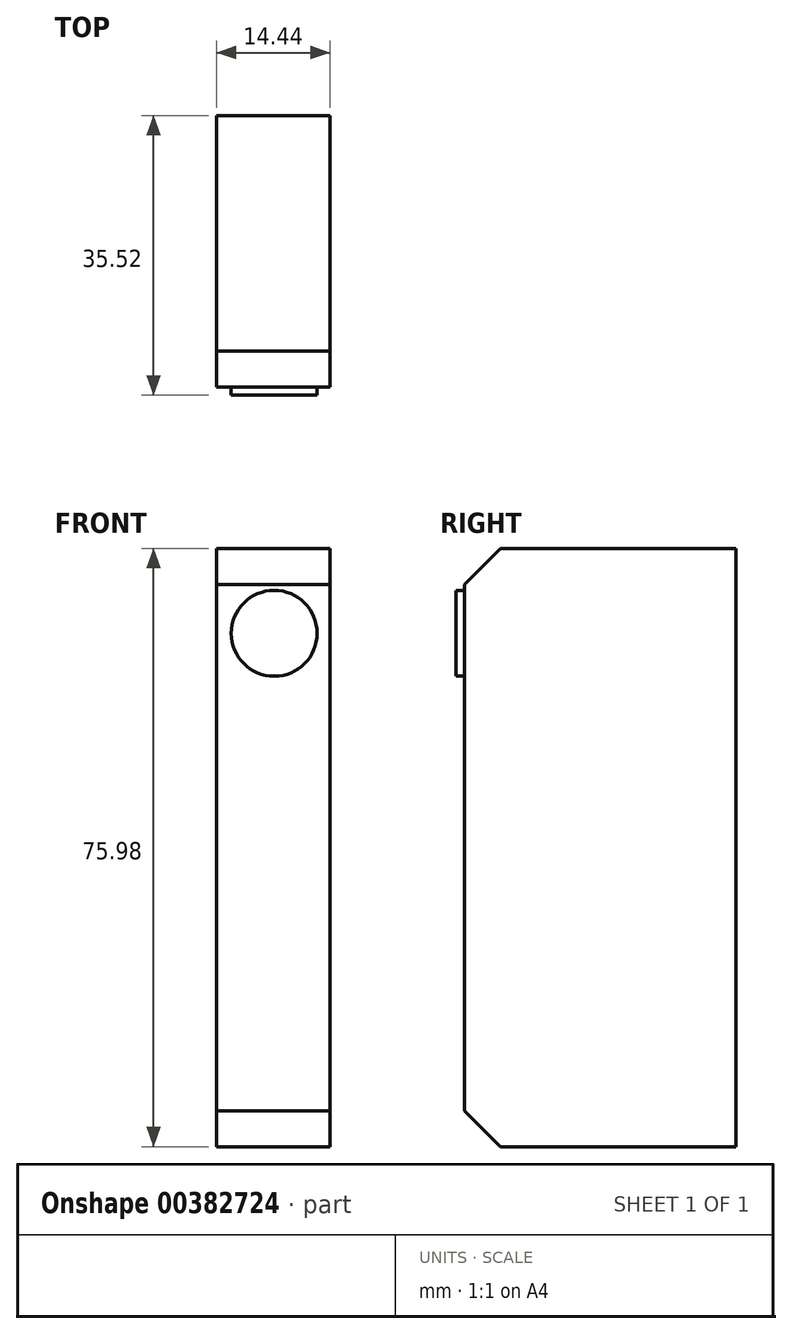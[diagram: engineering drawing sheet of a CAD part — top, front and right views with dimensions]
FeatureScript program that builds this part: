
annotation { "Feature Type Name" : "Feature", "Feature Type Description" : "" }
export const myFeature = defineFeature(function(context is Context, id is Id, definition is map)
    precondition{}
    {
        {
            var Q0;
            Q0=qCreatedBy(makeId("Front.planeOp"),FACE);
            var sketch = newSketch(context, id + "F0", { "sketchPlane" : qUnion([Q0])});
            skLineSegment(sketch, "E0.bottom", {"start": v(0, 75.98) * mm, "end": v(14.44, 75.98) * mm});
            skLineSegment(sketch, "E0.top", {"start": v(0, 0) * mm, "end": v(14.44, 0) * mm});
            skLineSegment(sketch, "E0.left", {"start": v(0, 75.98) * mm, "end": v(0, 0) * mm});
            skLineSegment(sketch, "E0.right", {"start": v(14.44, 75.98) * mm, "end": v(14.44, 0) * mm});
            skSolve(sketch);
        }
        {
            var Q0;
            Q0 = qSketchRegion(id + "F0", true);
            extrude(context, id + "F1", {"entities" : qUnion([Q0]), "oppositeDirection" : true, "depth" : 34.48 * mm});
        }
        {
            var Q0;
            Q0=makeQuery(id+"F1.opExtrude","CAP_FACE",FACE,{"disambiguationData":[OSD([sQuery(id+"F0.wireOp",EDGE,"E0.bottom"),sQuery(id+"F0.wireOp",EDGE,"E0.top"),sQuery(id+"F0.wireOp",EDGE,"E0.left"),sQuery(id+"F0.wireOp",EDGE,"E0.right")])],"isStart":true});
            var sketch = newSketch(context, id + "F2", { "sketchPlane" : qUnion([Q0])});
            skCircle(sketch, "E1", {"center": v(7.33, 65.21) * mm, "radius": 5.45 * mm});
            skSolve(sketch);
        }
        {
            var Q0;
            Q0=makeQuery(id+"F2.imprint","IMPRINT",FACE,{"disambiguationData":[TD([[makeQuery(id+"F2.imprint","IMPRINT",EDGE,{"derivedFrom":sQuery(id+"F2.wireOp",EDGE,"E1")}),1.0]])]});
            extrude(context, id + "F3", {"entities" : qUnion([Q0]), "operationType" : NewBodyOperationType.ADD, "depth" : 1.04 * mm});
        }
        {
            var Q0;
            Q0=makeQuery(id+"F1.opExtrude","CAP_EDGE",EDGE,{"disambiguationData":[OSD([sQuery(id+"F0.wireOp",EDGE,"E0.bottom")])],"isStart":true});
            var Q1;
            Q1=makeQuery(id+"F1.opExtrude","CAP_EDGE",EDGE,{"disambiguationData":[OSD([sQuery(id+"F0.wireOp",EDGE,"E0.top")])],"isStart":true});
            chamfer(context, id + "F4", {"entities" : qUnion([Q0, Q1]), "width" : 4.57 * mm, "tangentPropagation" : true});
        }
    });
